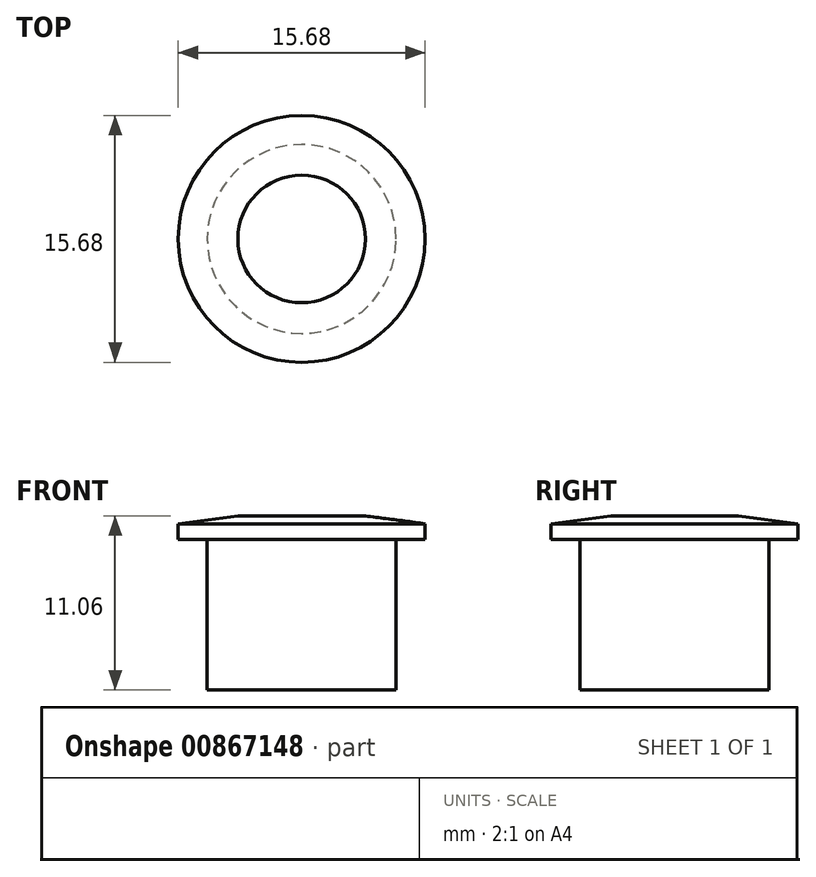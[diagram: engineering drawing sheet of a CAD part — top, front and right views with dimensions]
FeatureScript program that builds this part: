
annotation { "Feature Type Name" : "Feature", "Feature Type Description" : "" }
export const myFeature = defineFeature(function(context is Context, id is Id, definition is map)
    precondition{}
    {
        {
            var Q0;
            Q0=qCreatedBy(makeId("Front.planeOp"),FACE);
            var sketch = newSketch(context, id + "F0", { "sketchPlane" : qUnion([Q0])});
            skLineSegment(sketch, "E0", {"start": v(0, 18.29) * mm, "end": v(-4.05, 18.29) * mm});
            skLineSegment(sketch, "E1", {"start": v(-4.05, 18.29) * mm, "end": v(-7.84, 17.79) * mm});
            skLineSegment(sketch, "E2", {"start": v(-7.84, 17.79) * mm, "end": v(-7.84, 16.79) * mm});
            skLineSegment(sketch, "E3", {"start": v(-7.84, 16.79) * mm, "end": v(-6, 16.79) * mm});
            skLineSegment(sketch, "E4", {"start": v(-6, 16.79) * mm, "end": v(-6, 7.23) * mm});
            skLineSegment(sketch, "E5", {"start": v(-6, 7.23) * mm, "end": v(0, 7.23) * mm});
            skLineSegment(sketch, "E6", {"start": v(0, 43.48) * mm, "end": v(0, -35.72) * mm, "construction": true});
            skLineSegment(sketch, "E7", {"start": v(0, 18.29) * mm, "end": v(0, 7.23) * mm});
            skSolve(sketch);
        }
        {
            var Q0;
            Q0=qSketchRegion(id+"F0",true);
            var Q1;
            Q1=sQuery(id+"F0.wireOp",EDGE,"E6");
            revolve(context, id + "F1", {"surfaceOperationType" : NewSurfaceOperationType.NEW, "entities" : qUnion([Q0]), "axis" : qUnion([Q1]), "revolveType" : RevolveType.FULL});
        }
    });
